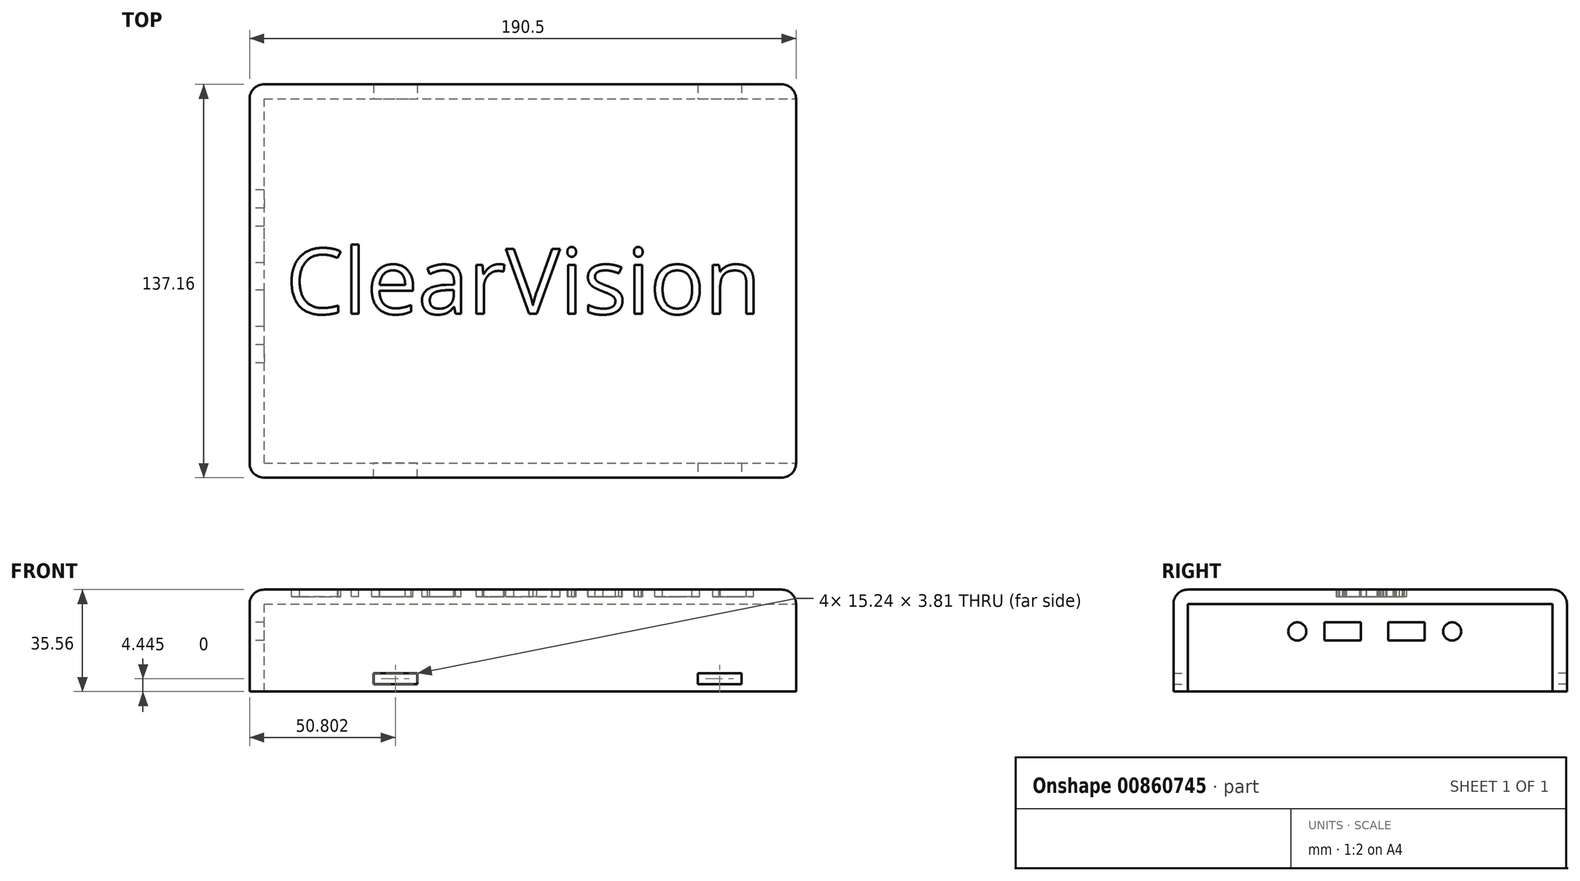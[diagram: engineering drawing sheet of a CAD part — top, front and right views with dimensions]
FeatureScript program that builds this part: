
annotation { "Feature Type Name" : "Feature", "Feature Type Description" : "" }
export const myFeature = defineFeature(function(context is Context, id is Id, definition is map)
    precondition{}
    {
        {
            var Q0;
            Q0=qCreatedBy(makeId("Top.planeOp"),FACE);
            var sketch = newSketch(context, id + "F0", { "sketchPlane" : qUnion([Q0])});
            skLineSegment(sketch, "E0.bottom", {"start": v(-147.94, 72.5) * mm, "end": v(42.56, 72.5) * mm});
            skLineSegment(sketch, "E0.top", {"start": v(-147.94, -64.66) * mm, "end": v(42.56, -64.66) * mm});
            skLineSegment(sketch, "E0.left", {"start": v(-147.94, 72.5) * mm, "end": v(-147.94, -64.66) * mm});
            skLineSegment(sketch, "E0.right", {"start": v(42.56, 72.5) * mm, "end": v(42.56, -64.66) * mm});
            skSolve(sketch);
        }
        {
            var Q0;
            Q0 = qSketchRegion(id + "F0", true);
            extrude(context, id + "F1", {"entities" : qUnion([Q0]), "depth" : 5.08 * mm, "offsetDistance" : 25.4 * mm});
        }
        {
            var Q0;
            Q0=makeQuery(id+"F1.opExtrude","CAP_FACE",FACE,{"disambiguationData":[OSD([sQuery(id+"F0.wireOp",EDGE,"E0.bottom"),sQuery(id+"F0.wireOp",EDGE,"E0.top"),sQuery(id+"F0.wireOp",EDGE,"E0.left"),sQuery(id+"F0.wireOp",EDGE,"E0.right")])],"isStart":false});
            var sketch = newSketch(context, id + "F2", { "sketchPlane" : qUnion([Q0])});
            skText(sketch, "E1", { "text": "ClearVision", "fontName": "OpenSans-Regular.ttf"});
            const initialGuessF2  = {"E1": [-0.13524, -0.00753, 1, 0, 0.0229]};
            skSetInitialGuess(sketch, initialGuessF2);
            skSolve(sketch);
        }
        {
            var Q0;
            Q0 = qSketchRegion(id + "F2", true);
            extrude(context, id + "F3", {"entities" : qUnion([Q0]), "operationType" : NewBodyOperationType.REMOVE, "oppositeDirection" : true, "depth" : 2.54 * mm, "offsetDistance" : 25.4 * mm});
        }
        {
            var Q0;
            Q0=makeQuery(id+"F1.opExtrude","CAP_EDGE",EDGE,{"disambiguationData":[OSD([sQuery(id+"F0.wireOp",EDGE,"E0.left")])],"isStart":false});
            var Q1;
            Q1=makeQuery(id+"F1.opExtrude","CAP_EDGE",EDGE,{"disambiguationData":[OSD([sQuery(id+"F0.wireOp",EDGE,"E0.top")])],"isStart":false});
            var Q2;
            Q2=makeQuery(id+"F1.opExtrude","CAP_EDGE",EDGE,{"disambiguationData":[OSD([sQuery(id+"F0.wireOp",EDGE,"E0.bottom")])],"isStart":false});
            fillet(context, id + "F4", {"entities" : qUnion([Q0, Q1, Q2]), "radius" : 5.08 * mm, "tangentPropagation" : true, "allowEdgeOverflow" : false});
        }
        {
            var Q0;
            Q0=makeQuery(id+"F4.opFillet","BLEND_EDGE",EDGE,{"blendedFrom":[makeQuery(id+"F1.opExtrude","CAP_EDGE",EDGE,{"disambiguationData":[OSD([sQuery(id+"F0.wireOp",EDGE,"E0.top")])],"isStart":false}),makeQuery(id+"F1.opExtrude","CAP_EDGE",EDGE,{"disambiguationData":[OSD([sQuery(id+"F0.wireOp",EDGE,"E0.left")])],"isStart":false})],"blendedInto":[]});
            var Q1;
            Q1=makeQuery(id+"F4.opFillet","BLEND_EDGE",EDGE,{"blendedFrom":[makeQuery(id+"F1.opExtrude","CAP_EDGE",EDGE,{"disambiguationData":[OSD([sQuery(id+"F0.wireOp",EDGE,"E0.top")])],"isStart":false}),makeQuery(id+"F1.opExtrude","CAP_EDGE",EDGE,{"disambiguationData":[OSD([sQuery(id+"F0.wireOp",EDGE,"E0.right")])],"isStart":false})],"blendedInto":[]});
            var Q2;
            Q2=makeQuery(id+"F4.opFillet","BLEND_EDGE",EDGE,{"blendedFrom":[makeQuery(id+"F1.opExtrude","CAP_EDGE",EDGE,{"disambiguationData":[OSD([sQuery(id+"F0.wireOp",EDGE,"E0.bottom")])],"isStart":false}),makeQuery(id+"F1.opExtrude","CAP_EDGE",EDGE,{"disambiguationData":[OSD([sQuery(id+"F0.wireOp",EDGE,"E0.right")])],"isStart":false})],"blendedInto":[]});
            var Q3;
            Q3=makeQuery(id+"F4.opFillet","BLEND_EDGE",EDGE,{"blendedFrom":[makeQuery(id+"F1.opExtrude","CAP_EDGE",EDGE,{"disambiguationData":[OSD([sQuery(id+"F0.wireOp",EDGE,"E0.bottom")])],"isStart":false}),makeQuery(id+"F1.opExtrude","CAP_EDGE",EDGE,{"disambiguationData":[OSD([sQuery(id+"F0.wireOp",EDGE,"E0.left")])],"isStart":false})],"blendedInto":[]});
            fillet(context, id + "F5", {"entities" : qUnion([Q0, Q1, Q2, Q3]), "radius" : 5.08 * mm, "tangentPropagation" : true, "allowEdgeOverflow" : false});
        }
        {
            var Q0;
            Q0=makeQuery(id+"F1.opExtrude","CAP_FACE",FACE,{"disambiguationData":[OSD([sQuery(id+"F0.wireOp",EDGE,"E0.bottom"),sQuery(id+"F0.wireOp",EDGE,"E0.top"),sQuery(id+"F0.wireOp",EDGE,"E0.left"),sQuery(id+"F0.wireOp",EDGE,"E0.right")])],"isStart":true});
            var sketch = newSketch(context, id + "F6", { "sketchPlane" : qUnion([Q0])});
            skLineSegment(sketch, "E2", {"start": v(-142.86, 59.58) * mm, "end": v(-142.86, -67.42) * mm});
            skLineSegment(sketch, "E3", {"start": v(-142.86, -67.42) * mm, "end": v(-2.1, -67.42) * mm});
            skLineSegment(sketch, "E4", {"start": v(-142.86, 59.58) * mm, "end": v(-8.67, 59.58) * mm});
            skLineSegment(sketch, "E5", {"start": v(-8.67, 59.58) * mm, "end": v(42.56, 59.58) * mm});
            skLineSegment(sketch, "E6", {"start": v(-2.1, -67.42) * mm, "end": v(42.56, -67.42) * mm});
            skSolve(sketch);
        }
        {
            var Q0;
            Q0=makeQuery(id+"F6.imprint","IMPRINT",FACE,{"disambiguationData":[TD([[makeQuery(id+"F6.imprint","IMPRINT",EDGE,{"derivedFrom":sQuery(id+"F6.wireOp",EDGE,"E2")}),-1.0]])]});
            extrude(context, id + "F7", {"entities" : qUnion([Q0]), "operationType" : NewBodyOperationType.ADD, "depth" : 30.48 * mm, "offsetDistance" : 25.4 * mm});
        }
        {
            var Q0;
            {var subQ0=sQuery(id+"F0.wireOp",EDGE,"E0.right");var subQ1=sQuery(id+"F0.wireOp",EDGE,"E0.left");var subQ2=sQuery(id+"F0.wireOp",EDGE,"E0.top");var subQ3=sQuery(id+"F0.wireOp",EDGE,"E0.bottom");Q0=makeQuery(id+"F7.opExtrude","SWEPT_FACE",FACE,{"disambiguationData":[OSD([subQ3,subQ2,subQ1,subQ0]),TDD([makeQuery(id+"F6.imprint","IMPRINT",EDGE,{"derivedFrom":makeQuery(id+"F4.opFillet","BLEND_EDGE",EDGE,{"blendedFrom":[makeQuery(id+"F1.opExtrude","CAP_EDGE",EDGE,{"disambiguationData":[OSD([subQ1])],"isStart":false}),makeQuery(id+"F1.opExtrude","CAP_FACE",FACE,{"disambiguationData":[OSD([subQ3,subQ2,subQ1,subQ0])],"isStart":true})],"blendedInto":[makeQuery(id+"F1.opExtrude","CAP_FACE",FACE,{"disambiguationData":[OSD([subQ3,subQ2,subQ1,subQ0])],"isStart":true})]})})])]});}
            var sketch = newSketch(context, id + "F8", { "sketchPlane" : qUnion([Q0])});
            skCircle(sketch, "E7", {"center": v(-32.5, -9.53) * mm, "radius": 3.18 * mm});
            skLineSegment(sketch, "E8.bottom", {"start": v(-22.97, -6.35) * mm, "end": v(-10.27, -6.35) * mm});
            skLineSegment(sketch, "E8.top", {"start": v(-22.97, -12.7) * mm, "end": v(-10.27, -12.7) * mm});
            skLineSegment(sketch, "E8.left", {"start": v(-22.97, -6.35) * mm, "end": v(-22.97, -12.7) * mm});
            skLineSegment(sketch, "E8.right", {"start": v(-10.27, -6.35) * mm, "end": v(-10.27, -12.7) * mm});
            skLineSegment(sketch, "E9.bottom", {"start": v(-0.75, -6.35) * mm, "end": v(11.95, -6.35) * mm});
            skLineSegment(sketch, "E9.top", {"start": v(-0.75, -12.7) * mm, "end": v(11.95, -12.7) * mm});
            skLineSegment(sketch, "E9.left", {"start": v(-0.75, -6.35) * mm, "end": v(-0.75, -12.7) * mm});
            skLineSegment(sketch, "E9.right", {"start": v(11.95, -6.35) * mm, "end": v(11.95, -12.7) * mm});
            skCircle(sketch, "E10", {"center": v(21.48, -9.53) * mm, "radius": 3.18 * mm});
            skSolve(sketch);
        }
        {
            var Q0;
            Q0=makeQuery(id+"F8.imprint","IMPRINT",FACE,{"disambiguationData":[TD([[makeQuery(id+"F8.imprint","IMPRINT",EDGE,{"derivedFrom":sQuery(id+"F8.wireOp",EDGE,"E7")}),1.0]])]});
            var Q1;
            Q1=makeQuery(id+"F8.imprint","IMPRINT",FACE,{"disambiguationData":[TD([[makeQuery(id+"F8.imprint","IMPRINT",EDGE,{"derivedFrom":sQuery(id+"F8.wireOp",EDGE,"E8.bottom")}),-1.0]])]});
            var Q2;
            Q2=makeQuery(id+"F8.imprint","IMPRINT",FACE,{"disambiguationData":[TD([[makeQuery(id+"F8.imprint","IMPRINT",EDGE,{"derivedFrom":sQuery(id+"F8.wireOp",EDGE,"E9.bottom")}),-1.0]])]});
            var Q3;
            Q3=makeQuery(id+"F8.imprint","IMPRINT",FACE,{"disambiguationData":[TD([[makeQuery(id+"F8.imprint","IMPRINT",EDGE,{"derivedFrom":sQuery(id+"F8.wireOp",EDGE,"E10")}),1.0]])]});
            extrude(context, id + "F9", {"entities" : qUnion([Q0, Q1, Q2, Q3]), "operationType" : NewBodyOperationType.REMOVE, "oppositeDirection" : true, "depth" : 25.4 * mm, "offsetDistance" : 25.4 * mm});
        }
        {
            var Q0;
            Q0=makeQuery(id+"F7.opExtrude","SWEPT_FACE",FACE,{"disambiguationData":[OSD([sQuery(id+"F6.wireOp",EDGE,"E4"),sQuery(id+"F6.wireOp",EDGE,"E5")])]});
            var sketch = newSketch(context, id + "F10", { "sketchPlane" : qUnion([Q0])});
            skLineSegment(sketch, "E11.bottom", {"start": v(89.52, -24.13) * mm, "end": v(104.76, -24.13) * mm});
            skLineSegment(sketch, "E11.top", {"start": v(89.52, -27.94) * mm, "end": v(104.76, -27.94) * mm});
            skLineSegment(sketch, "E11.left", {"start": v(89.52, -24.13) * mm, "end": v(89.52, -27.94) * mm});
            skLineSegment(sketch, "E11.right", {"start": v(104.76, -24.13) * mm, "end": v(104.76, -27.94) * mm});
            skSolve(sketch);
        }
        {
            var Q0;
            Q0=makeQuery(id+"F10.imprint","IMPRINT",FACE,{"disambiguationData":[TD([[makeQuery(id+"F10.imprint","IMPRINT",EDGE,{"derivedFrom":sQuery(id+"F10.wireOp",EDGE,"E11.bottom")}),-1.0]])]});
            extrude(context, id + "F11", {"entities" : qUnion([Q0]), "operationType" : NewBodyOperationType.REMOVE, "oppositeDirection" : true, "depth" : 25.4 * mm, "offsetDistance" : 25.4 * mm});
        }
        {
            var Q0;
            Q0=makeQuery(id+"F7.opExtrude","SWEPT_FACE",FACE,{"disambiguationData":[OSD([sQuery(id+"F6.wireOp",EDGE,"E3"),sQuery(id+"F6.wireOp",EDGE,"E6")])]});
            var sketch = newSketch(context, id + "F12", { "sketchPlane" : qUnion([Q0])});
            skLineSegment(sketch, "E12.bottom", {"start": v(-104.76, -24.13) * mm, "end": v(-89.52, -24.13) * mm});
            skLineSegment(sketch, "E12.top", {"start": v(-104.76, -27.94) * mm, "end": v(-89.52, -27.94) * mm});
            skLineSegment(sketch, "E12.left", {"start": v(-104.76, -24.13) * mm, "end": v(-104.76, -27.94) * mm});
            skLineSegment(sketch, "E12.right", {"start": v(-89.52, -24.13) * mm, "end": v(-89.52, -27.94) * mm});
            skSolve(sketch);
        }
        {
            var Q0;
            Q0=makeQuery(id+"F12.imprint","IMPRINT",FACE,{"disambiguationData":[TD([[makeQuery(id+"F12.imprint","IMPRINT",EDGE,{"derivedFrom":sQuery(id+"F12.wireOp",EDGE,"E12.bottom")}),-1.0]])]});
            extrude(context, id + "F13", {"entities" : qUnion([Q0]), "operationType" : NewBodyOperationType.REMOVE, "oppositeDirection" : true, "depth" : 25.4 * mm, "offsetDistance" : 25.4 * mm});
        }
        {
            var Q0;
            {var subQ0=sQuery(id+"F0.wireOp",EDGE,"E0.right");var subQ1=sQuery(id+"F0.wireOp",EDGE,"E0.left");var subQ2=sQuery(id+"F0.wireOp",EDGE,"E0.top");var subQ3=sQuery(id+"F0.wireOp",EDGE,"E0.bottom");Q0=makeQuery(id+"F7.opExtrude","SWEPT_FACE",FACE,{"disambiguationData":[OSD([subQ3,subQ2,subQ1,subQ0]),TDD([makeQuery(id+"F6.imprint","IMPRINT",EDGE,{"derivedFrom":makeQuery(id+"F4.opFillet","BLEND_EDGE",EDGE,{"blendedFrom":[makeQuery(id+"F1.opExtrude","CAP_EDGE",EDGE,{"disambiguationData":[OSD([subQ2])],"isStart":false}),makeQuery(id+"F1.opExtrude","CAP_FACE",FACE,{"disambiguationData":[OSD([subQ3,subQ2,subQ1,subQ0])],"isStart":true})],"blendedInto":[makeQuery(id+"F1.opExtrude","CAP_FACE",FACE,{"disambiguationData":[OSD([subQ3,subQ2,subQ1,subQ0])],"isStart":true})]})})])]});}
            var sketch = newSketch(context, id + "F14", { "sketchPlane" : qUnion([Q0])});
            skLineSegment(sketch, "E13.bottom", {"start": v(8.27, -24.13) * mm, "end": v(23.51, -24.13) * mm});
            skLineSegment(sketch, "E13.top", {"start": v(8.27, -27.94) * mm, "end": v(23.51, -27.94) * mm});
            skLineSegment(sketch, "E13.left", {"start": v(8.27, -24.13) * mm, "end": v(8.27, -27.94) * mm});
            skLineSegment(sketch, "E13.right", {"start": v(23.51, -24.13) * mm, "end": v(23.51, -27.94) * mm});
            skSolve(sketch);
        }
        {
            var Q0;
            Q0=makeQuery(id+"F14.imprint","IMPRINT",FACE,{"disambiguationData":[TD([[makeQuery(id+"F14.imprint","IMPRINT",EDGE,{"derivedFrom":sQuery(id+"F14.wireOp",EDGE,"E13.bottom")}),-1.0]])]});
            extrude(context, id + "F15", {"entities" : qUnion([Q0]), "operationType" : NewBodyOperationType.REMOVE, "oppositeDirection" : true, "depth" : 25.4 * mm, "offsetDistance" : 25.4 * mm});
        }
        {
            var Q0;
            Q0=makeQuery(id+"F7.opExtrude","SWEPT_FACE",FACE,{"disambiguationData":[OSD([sQuery(id+"F6.wireOp",EDGE,"E3"),sQuery(id+"F6.wireOp",EDGE,"E6")])]});
            var sketch = newSketch(context, id + "F16", { "sketchPlane" : qUnion([Q0])});
            skLineSegment(sketch, "E14.bottom", {"start": v(8.27, -24.13) * mm, "end": v(23.51, -24.13) * mm});
            skLineSegment(sketch, "E14.top", {"start": v(8.27, -27.94) * mm, "end": v(23.51, -27.94) * mm});
            skLineSegment(sketch, "E14.left", {"start": v(8.27, -24.13) * mm, "end": v(8.27, -27.94) * mm});
            skLineSegment(sketch, "E14.right", {"start": v(23.51, -24.13) * mm, "end": v(23.51, -27.94) * mm});
            skSolve(sketch);
        }
        {
            var Q0;
            Q0=makeQuery(id+"F16.imprint","IMPRINT",FACE,{"disambiguationData":[TD([[makeQuery(id+"F16.imprint","IMPRINT",EDGE,{"derivedFrom":sQuery(id+"F16.wireOp",EDGE,"E14.bottom")}),-1.0]])]});
            extrude(context, id + "F17", {"entities" : qUnion([Q0]), "operationType" : NewBodyOperationType.REMOVE, "oppositeDirection" : true, "depth" : 25.4 * mm, "offsetDistance" : 25.4 * mm});
        }
        {
            var Q0;
            {var subQ0=sQuery(id+"F0.wireOp",EDGE,"E0.right");var subQ1=sQuery(id+"F0.wireOp",EDGE,"E0.left");var subQ2=sQuery(id+"F0.wireOp",EDGE,"E0.top");var subQ3=sQuery(id+"F0.wireOp",EDGE,"E0.bottom");Q0=makeQuery(id+"F7.opExtrude","SWEPT_EDGE",EDGE,{"disambiguationData":[OSD([subQ3,subQ2,subQ1,subQ0]),TDD([makeQuery(id+"F6.imprint","INTERSECT",VERTEX,{"derivedFrom":[makeQuery(id+"F1.opExtrude","CAP_EDGE",EDGE,{"disambiguationData":[OSD([subQ0])],"isStart":true}),makeQuery(id+"F4.opFillet","BLEND_EDGE",EDGE,{"blendedFrom":[makeQuery(id+"F1.opExtrude","CAP_EDGE",EDGE,{"disambiguationData":[OSD([subQ2])],"isStart":false}),makeQuery(id+"F1.opExtrude","CAP_FACE",FACE,{"disambiguationData":[OSD([subQ3,subQ2,subQ1,subQ0])],"isStart":true})],"blendedInto":[makeQuery(id+"F1.opExtrude","CAP_FACE",FACE,{"disambiguationData":[OSD([subQ3,subQ2,subQ1,subQ0])],"isStart":true})]})]})])]});}
            fillet(context, id + "F18", {"entities" : qUnion([Q0]), "radius" : 5.08 * mm, "tangentPropagation" : true, "allowEdgeOverflow" : false});
        }
    });
